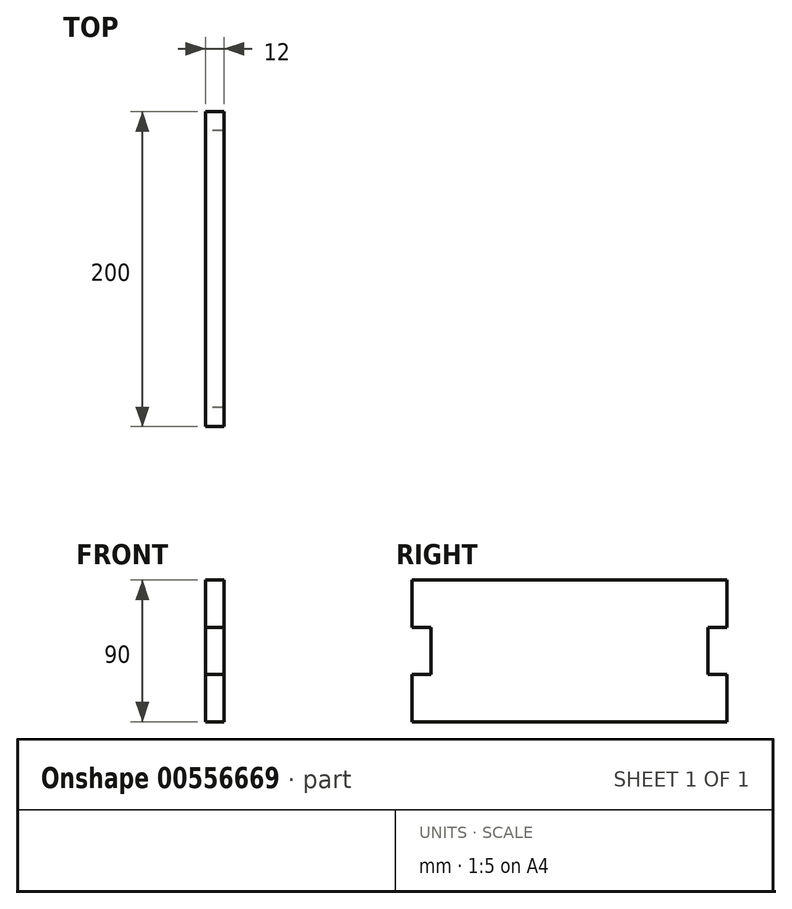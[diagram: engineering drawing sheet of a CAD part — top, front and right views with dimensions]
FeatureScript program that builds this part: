
annotation { "Feature Type Name" : "Feature", "Feature Type Description" : "" }
export const myFeature = defineFeature(function(context is Context, id is Id, definition is map)
    precondition{}
    {
        {
            var Q0;
            Q0=qCreatedBy(makeId("Right.planeOp"),FACE);
            var sketch = newSketch(context, id + "F0", { "sketchPlane" : qUnion([Q0])});
            skLineSegment(sketch, "E0", {"start": v(0, 0) * mm, "end": v(0, 30) * mm});
            skLineSegment(sketch, "E1", {"start": v(0, 30) * mm, "end": v(12, 30) * mm});
            skLineSegment(sketch, "E2", {"start": v(12, 30) * mm, "end": v(12, 60) * mm});
            skLineSegment(sketch, "E3", {"start": v(0, 60) * mm, "end": v(12, 60) * mm});
            skLineSegment(sketch, "E4", {"start": v(0, 0) * mm, "end": v(100, 0) * mm});
            skLineSegment(sketch, "E5", {"start": v(0, 60) * mm, "end": v(0, 90) * mm});
            skLineSegment(sketch, "E6", {"start": v(0, 90) * mm, "end": v(100, 90) * mm});
            skLineSegment(sketch, "E7", {"start": v(100, 90) * mm, "end": v(100, 0) * mm, "construction": true});
            skLineSegment(sketch, "E8.MirrorCS", {"start": v(200, 0) * mm, "end": v(100, 0) * mm});
            skLineSegment(sketch, "E9.MirrorCS", {"start": v(200, 60) * mm, "end": v(188, 60) * mm});
            skLineSegment(sketch, "E10.MirrorCS", {"start": v(200, 30) * mm, "end": v(188, 30) * mm});
            skLineSegment(sketch, "E11.MirrorCS", {"start": v(188, 30) * mm, "end": v(188, 60) * mm});
            skLineSegment(sketch, "E12.MirrorCS", {"start": v(200, 0) * mm, "end": v(200, 30) * mm});
            skLineSegment(sketch, "E13.MirrorCS", {"start": v(200, 60) * mm, "end": v(200, 90) * mm});
            skLineSegment(sketch, "E14.MirrorCS", {"start": v(200, 90) * mm, "end": v(100, 90) * mm});
            skSolve(sketch);
        }
        {
            var Q0;
            Q0 = qSketchRegion(id + "F0", true);
            extrude(context, id + "F1", {"entities" : qUnion([Q0]), "depth" : 12 * mm, "offsetDistance" : 25 * mm});
        }
    });
